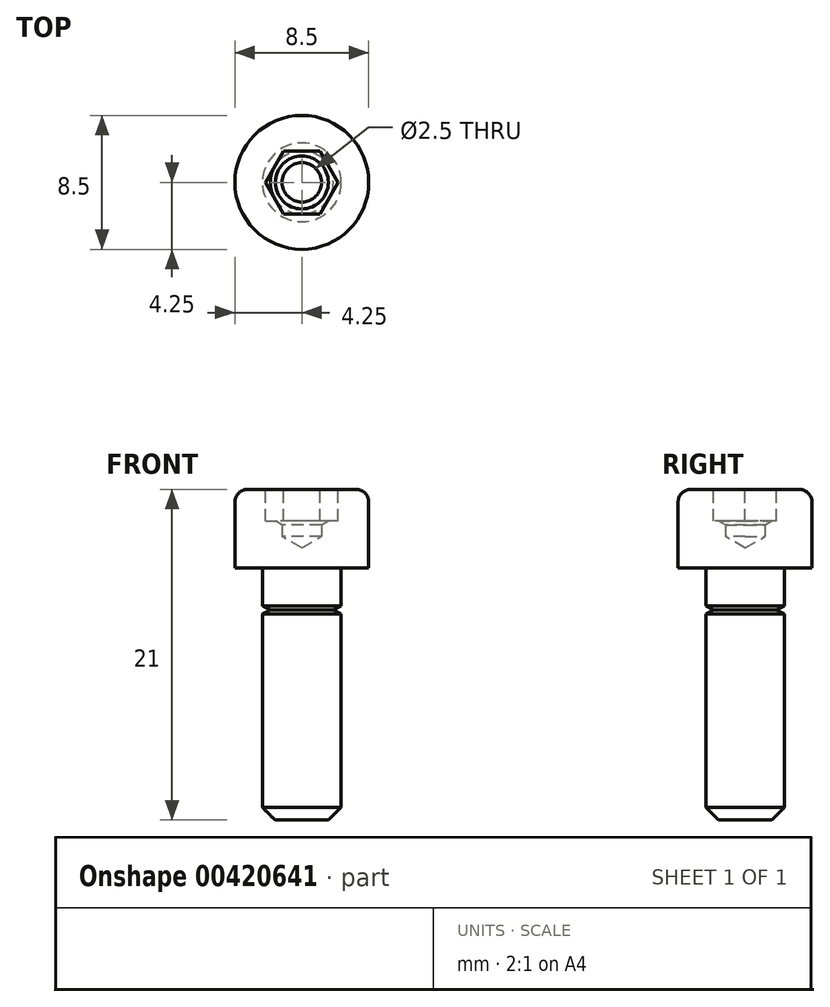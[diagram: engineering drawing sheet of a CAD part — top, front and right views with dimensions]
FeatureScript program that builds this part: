
annotation { "Feature Type Name" : "Feature", "Feature Type Description" : "" }
export const myFeature = defineFeature(function(context is Context, id is Id, definition is map)
    precondition{}
    {
        {
            var Q0;
            Q0=qCreatedBy(makeId("Front.planeOp"),FACE);
            var sketch = newSketch(context, id + "F0", { "sketchPlane" : qUnion([Q0])});
            skLineSegment(sketch, "E0", {"start": v(0, 0) * mm, "end": v(0, 36.66) * mm, "construction": true});
            skLineSegment(sketch, "E1", {"start": v(0, 0) * mm, "end": v(-2.5, 0) * mm});
            skLineSegment(sketch, "E2", {"start": v(-2.5, 0) * mm, "end": v(-2.5, 16) * mm, "construction": true});
            skLineSegment(sketch, "E3", {"start": v(-2.5, 16) * mm, "end": v(-4.25, 16) * mm});
            skLineSegment(sketch, "E4", {"start": v(-4.25, 16) * mm, "end": v(-4.25, 21) * mm});
            skLineSegment(sketch, "E5", {"start": v(-4.25, 21) * mm, "end": v(0, 21) * mm, "construction": true});
            skLineSegment(sketch, "E6", {"start": v(-1.25, 21) * mm, "end": v(-1.25, 18) * mm});
            skLineSegment(sketch, "E7", {"start": v(-1.25, 18) * mm, "end": v(0, 17.28) * mm});
            skLineSegment(sketch, "E8", {"start": v(0, 17.28) * mm, "end": v(0, 0) * mm});
            skLineSegment(sketch, "E9", {"start": v(-1.25, 21) * mm, "end": v(-4.25, 21) * mm});
            skLineSegment(sketch, "E10", {"start": v(-2.5, 13.6) * mm, "end": v(-2, 13.35) * mm});
            skLineSegment(sketch, "E11", {"start": v(-2, 13.35) * mm, "end": v(-2.5, 13.1) * mm});
            skLineSegment(sketch, "E12", {"start": v(-2.5, 13.1) * mm, "end": v(-2.5, 0) * mm});
            skLineSegment(sketch, "E13", {"start": v(-2.5, 13.6) * mm, "end": v(-2.5, 16) * mm});
            skSolve(sketch);
        }
        {
            var Q0;
            Q0=qSketchRegion(id+"F0",true);
            var Q1;
            Q1=sQuery(id+"F0.wireOp",EDGE,"E0");
            revolve(context, id + "F1", {"entities" : qUnion([Q0]), "axis" : qUnion([Q1]), "revolveType" : RevolveType.FULL});
        }
        {
            var Q0;
            Q0=makeQuery(id+"F1.opRevolve","SWEPT_EDGE",EDGE,{"disambiguationData":[OSD([sQuery(id+"F0.wireOp",EDGE,"E4"),sQuery(id+"F0.wireOp",EDGE,"E9")])]});
            fillet(context, id + "F2", {"entities" : qUnion([Q0]), "radius" : 0.8 * mm, "tangentPropagation" : true, "allowEdgeOverflow" : false});
        }
        {
            var Q0;
            Q0=makeQuery(id+"F1.opRevolve","SWEPT_EDGE",EDGE,{"disambiguationData":[OSD([sQuery(id+"F0.wireOp",EDGE,"E1"),sQuery(id+"F0.wireOp",EDGE,"E2")])]});
            chamfer(context, id + "F3", {"entities" : qUnion([Q0]), "width" : 0.8 * mm, "tangentPropagation" : true});
        }
        {
            var Q0;
            Q0=makeQuery(id+"F1.opRevolve","SWEPT_FACE",FACE,{"disambiguationData":[OSD([sQuery(id+"F0.wireOp",EDGE,"E9")])]});
            var sketch = newSketch(context, id + "F4", { "sketchPlane" : qUnion([Q0])});
            skCircle(sketch, "E14.cCircle", {"center": v(0, 0) * mm, "radius": 2 * mm, "construction": true});
            skLineSegment(sketch, "E14.0", {"start": v(1.15, -2) * mm, "end": v(-1.15, -2) * mm});
            skLineSegment(sketch, "E14.1", {"start": v(-1.15, -2) * mm, "end": v(-2.3, 0) * mm});
            skLineSegment(sketch, "E14.2", {"start": v(-2.3, 0) * mm, "end": v(-1.15, 2) * mm});
            skLineSegment(sketch, "E14.3", {"start": v(-1.15, 2) * mm, "end": v(1.15, 2) * mm});
            skLineSegment(sketch, "E14.4", {"start": v(1.15, 2) * mm, "end": v(2.3, 0) * mm});
            skLineSegment(sketch, "E14.5", {"start": v(2.3, 0) * mm, "end": v(1.15, -2) * mm});
            skPoint(sketch, "E14.0.midPoint", {"position": v(0, -2) * mm});
            skSolve(sketch);
        }
        {
            var Q0;
            Q0=qSketchRegion(id+"F4",true);
            extrude(context, id + "F5", {"entities" : qUnion([Q0]), "operationType" : NewBodyOperationType.REMOVE, "oppositeDirection" : true, "depth" : 2 * mm, "offsetDistance" : 25 * mm});
        }
        {
            var Q0;
            Q0=makeQuery(id+"F5.boolean.opBoolean","INTERSECT",EDGE,{"derivedFrom":[makeQuery(id+"F1.opRevolve","SWEPT_FACE",FACE,{"disambiguationData":[OSD([sQuery(id+"F0.wireOp",EDGE,"E6")])]}),makeQuery(id+"F5.opExtrude","CAP_FACE",FACE,{"disambiguationData":[OSD([sQuery(id+"F4.wireOp",EDGE,"E14.0"),sQuery(id+"F4.wireOp",EDGE,"E14.1"),sQuery(id+"F4.wireOp",EDGE,"E14.2"),sQuery(id+"F4.wireOp",EDGE,"E14.3"),sQuery(id+"F4.wireOp",EDGE,"E14.4"),sQuery(id+"F4.wireOp",EDGE,"E14.5")])],"isStart":false})]});
            chamfer(context, id + "F6", {"entities" : qUnion([Q0]), "chamferType" : ChamferType.OFFSET_ANGLE, "width" : 0.25 * mm, "oppositeDirection" : false, "angle" : 60 * degree, "tangentPropagation" : true});
        }
    });
